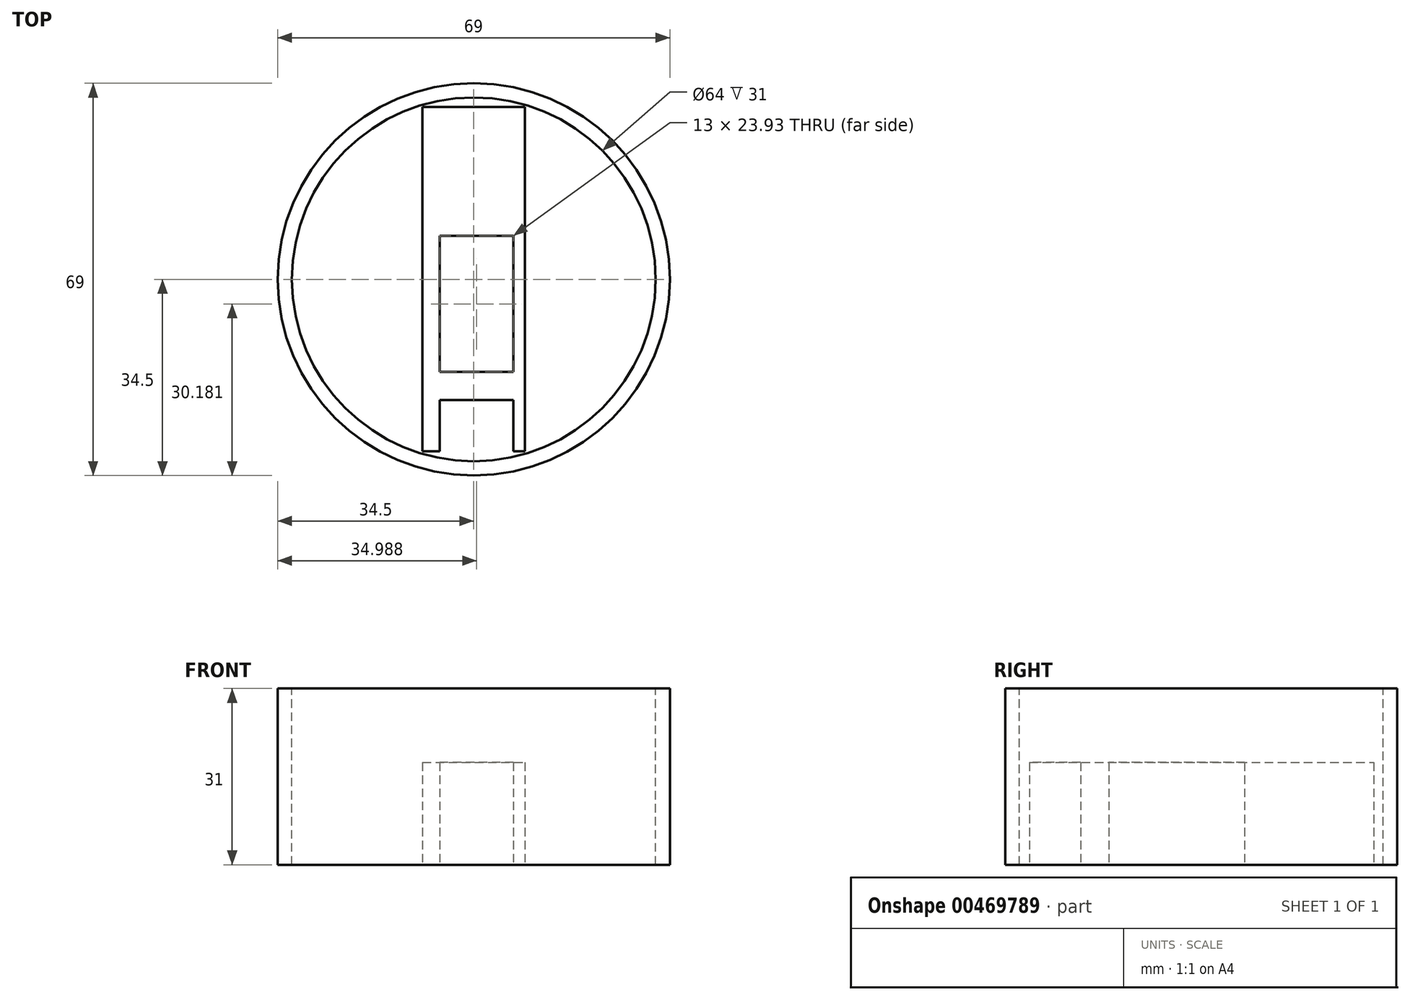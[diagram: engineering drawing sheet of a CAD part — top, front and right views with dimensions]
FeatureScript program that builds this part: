
annotation { "Feature Type Name" : "Feature", "Feature Type Description" : "" }
export const myFeature = defineFeature(function(context is Context, id is Id, definition is map)
    precondition{}
    {
        {
            var Q0;
            Q0=qCreatedBy(makeId("Top.planeOp"),FACE);
            var sketch = newSketch(context, id + "F0", { "sketchPlane" : qUnion([Q0])});
            skCircle(sketch, "E0", {"center": v(0, 0) * mm, "radius": 34.5 * mm});
            skSolve(sketch);
        }
        {
            var Q0;
            Q0 = qSketchRegion(id + "F0", true);
            extrude(context, id + "F1", {"entities" : qUnion([Q0]), "depth" : 31 * mm});
        }
        {
            var Q0;
            Q0=makeQuery(id+"F1.opExtrude","CAP_FACE",FACE,{"disambiguationData":[OSD([sQuery(id+"F0.wireOp",EDGE,"E0")])],"isStart":false});
            var sketch = newSketch(context, id + "F2", { "sketchPlane" : qUnion([Q0])});
            skCircle(sketch, "E1", {"center": v(0, 0) * mm, "radius": 32 * mm});
            skSolve(sketch);
        }
        {
            var Q0;
            Q0 = qSketchRegion(id + "F2", true);
            extrude(context, id + "F3", {"entities" : qUnion([Q0]), "operationType" : NewBodyOperationType.REMOVE, "oppositeDirection" : true, "depth" : 32 * mm});
        }
        {
            var Q0;
            Q0=qCreatedBy(makeId("Top.planeOp"),FACE);
            var sketch = newSketch(context, id + "F4", { "sketchPlane" : qUnion([Q0])});
            skLineSegment(sketch, "E2.bottom", {"start": v(-9.01, -30.24) * mm, "end": v(8.99, -30.24) * mm});
            skLineSegment(sketch, "E2.top", {"start": v(-9.01, 30.36) * mm, "end": v(8.99, 30.36) * mm});
            skLineSegment(sketch, "E2.left", {"start": v(-9.01, -30.24) * mm, "end": v(-9.01, 30.36) * mm});
            skLineSegment(sketch, "E2.right", {"start": v(8.99, -30.24) * mm, "end": v(8.99, 30.36) * mm});
            skSolve(sketch);
        }
        {
            var Q0;
            Q0 = qSketchRegion(id + "F4", true);
            extrude(context, id + "F5", {"entities" : qUnion([Q0]), "depth" : 18 * mm});
        }
        {
            var Q0;
            Q0=makeQuery(id+"F5.opExtrude","CAP_FACE",FACE,{"disambiguationData":[OSD([sQuery(id+"F4.wireOp",EDGE,"E2.bottom"),sQuery(id+"F4.wireOp",EDGE,"E2.top"),sQuery(id+"F4.wireOp",EDGE,"E2.left"),sQuery(id+"F4.wireOp",EDGE,"E2.right")])],"isStart":true});
            var sketch = newSketch(context, id + "F6", { "sketchPlane" : qUnion([Q0])});
            skLineSegment(sketch, "E3", {"start": v(-9.01, 30.24) * mm, "end": v(-6.01, 30.24) * mm});
            skLineSegment(sketch, "E4.bottom", {"start": v(-6.01, 30.24) * mm, "end": v(6.99, 30.24) * mm});
            skLineSegment(sketch, "E4.top", {"start": v(-6.01, 21.24) * mm, "end": v(6.99, 21.24) * mm});
            skLineSegment(sketch, "E4.left", {"start": v(-6.01, 30.24) * mm, "end": v(-6.01, 21.24) * mm});
            skLineSegment(sketch, "E4.right", {"start": v(6.99, 30.24) * mm, "end": v(6.99, 21.24) * mm});
            skSolve(sketch);
        }
        {
            var Q0;
            Q0=makeQuery(id+"F6.imprint","IMPRINT",FACE,{"disambiguationData":[TD([[makeQuery(id+"F6.imprint","IMPRINT",EDGE,{"derivedFrom":sQuery(id+"F6.wireOp",EDGE,"E4.bottom")}),-1.0]])]});
            extrude(context, id + "F7", {"entities" : qUnion([Q0]), "operationType" : NewBodyOperationType.REMOVE, "oppositeDirection" : true, "depth" : 25 * mm});
        }
        {
            var Q0;
            Q0=makeQuery(id+"F5.opExtrude","CAP_FACE",FACE,{"disambiguationData":[OSD([sQuery(id+"F4.wireOp",EDGE,"E2.bottom"),sQuery(id+"F4.wireOp",EDGE,"E2.top"),sQuery(id+"F4.wireOp",EDGE,"E2.left"),sQuery(id+"F4.wireOp",EDGE,"E2.right")])],"isStart":true});
            var sketch = newSketch(context, id + "F8", { "sketchPlane" : qUnion([Q0])});
            skLineSegment(sketch, "E5", {"start": v(8.99, 21.28) * mm, "end": v(8.99, 16.28) * mm});
            skLineSegment(sketch, "E6.bottom", {"start": v(6.99, 16.28) * mm, "end": v(-6.01, 16.28) * mm});
            skLineSegment(sketch, "E6.top", {"start": v(6.99, -7.65) * mm, "end": v(-6.01, -7.65) * mm});
            skLineSegment(sketch, "E6.left", {"start": v(6.99, 16.28) * mm, "end": v(6.99, -7.65) * mm});
            skLineSegment(sketch, "E6.right", {"start": v(-6.01, 16.28) * mm, "end": v(-6.01, -7.65) * mm});
            skSolve(sketch);
        }
        {
            var Q0;
            Q0 = qSketchRegion(id + "F8", true);
            extrude(context, id + "F9", {"entities" : qUnion([Q0]), "operationType" : NewBodyOperationType.REMOVE, "oppositeDirection" : true, "depth" : 25 * mm});
        }
    });
